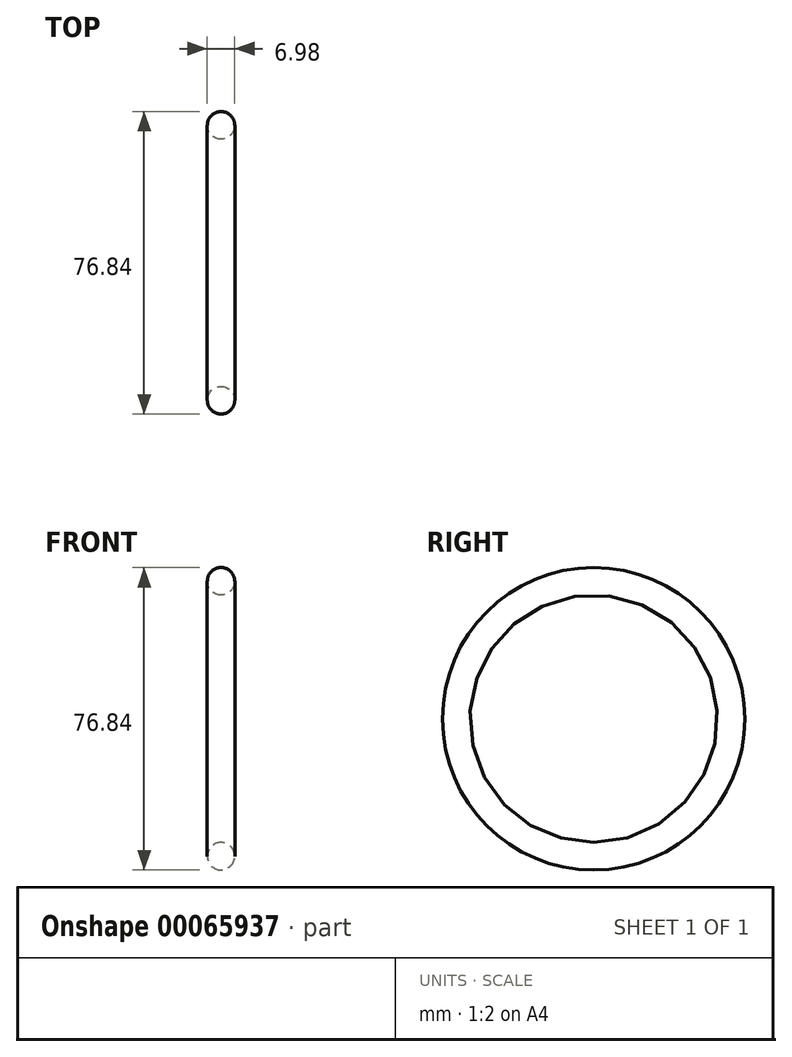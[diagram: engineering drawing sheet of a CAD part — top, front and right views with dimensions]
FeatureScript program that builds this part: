
annotation { "Feature Type Name" : "Feature", "Feature Type Description" : "" }
export const myFeature = defineFeature(function(context is Context, id is Id, definition is map)
    precondition{}
    {
        {
            var Q0;
            Q0=qCreatedBy(makeId("Front.planeOp"),FACE);
            var sketch = newSketch(context, id + "F0", { "sketchPlane" : qUnion([Q0])});
            skLineSegment(sketch, "E0", {"start": v(0, 0) * mm, "end": v(-6.06, 0) * mm, "construction": true});
            skCircle(sketch, "E1", {"center": v(0, 34.93) * mm, "radius": 3.5 * mm});
            skSolve(sketch);
        }
        {
            var Q0;
            Q0=makeQuery(id+"F0.imprint","IMPRINT",FACE,{"disambiguationData":[TD([[makeQuery(id+"F0.imprint","IMPRINT",EDGE,{"derivedFrom":sQuery(id+"F0.wireOp",EDGE,"E1")}),1.0]])]});
            var Q1;
            Q1=sQuery(id+"F0.wireOp",EDGE,"E0");
            revolve(context, id + "F1", {"entities" : qUnion([Q0]), "axis" : qUnion([Q1]), "revolveType" : RevolveType.FULL});
        }
    });
